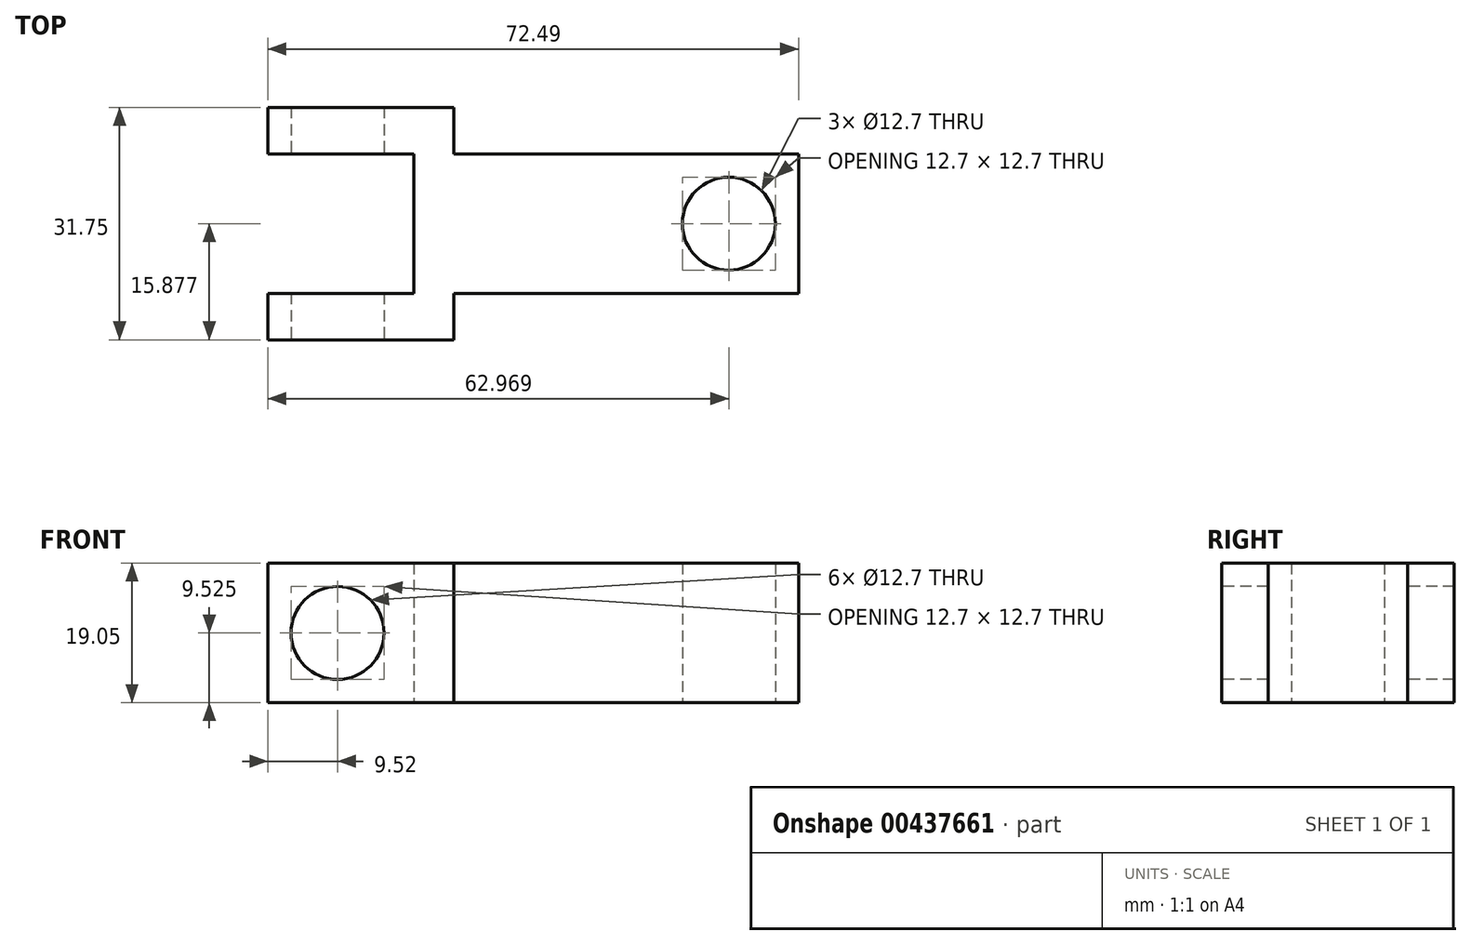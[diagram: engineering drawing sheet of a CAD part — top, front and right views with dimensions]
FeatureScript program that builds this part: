
annotation { "Feature Type Name" : "Feature", "Feature Type Description" : "" }
export const myFeature = defineFeature(function(context is Context, id is Id, definition is map)
    precondition{}
    {
        {
            var Q0;
            Q0=qCreatedBy(makeId("Top.planeOp"),FACE);
            var sketch = newSketch(context, id + "F0", { "sketchPlane" : qUnion([Q0])});
            skLineSegment(sketch, "E0.bottom", {"start": v(-1.7, -4.04) * mm, "end": v(45.4, -4.04) * mm});
            skLineSegment(sketch, "E0.top", {"start": v(-1.7, -23.09) * mm, "end": v(45.4, -23.09) * mm});
            skLineSegment(sketch, "E0.left", {"start": v(-27.1, 2.31) * mm, "end": v(-27.1, -4.04) * mm});
            skLineSegment(sketch, "E0.right", {"start": v(45.4, -4.04) * mm, "end": v(45.4, -23.09) * mm});
            skLineSegment(sketch, "E1", {"start": v(-27.1, 2.31) * mm, "end": v(-1.7, 2.31) * mm});
            skLineSegment(sketch, "E2", {"start": v(-27.1, -29.44) * mm, "end": v(-1.7, -29.44) * mm});
            skLineSegment(sketch, "E3", {"start": v(-1.7, -29.44) * mm, "end": v(-1.7, -23.09) * mm});
            skPoint(sketch, "E4.orphan", {"position": v(0, 2.31) * mm});
            skLineSegment(sketch, "E5.trimOffspring", {"start": v(-1.7, -4.04) * mm, "end": v(-1.7, 2.31) * mm});
            skLineSegment(sketch, "E6.bottom", {"start": v(-27.1, -4.04) * mm, "end": v(-7.15, -4.04) * mm});
            skLineSegment(sketch, "E6.top", {"start": v(-27.1, -23.09) * mm, "end": v(-7.15, -23.09) * mm});
            skLineSegment(sketch, "E6.right", {"start": v(-7.15, -4.04) * mm, "end": v(-7.15, -23.09) * mm});
            skLineSegment(sketch, "E7.trimOffspring", {"start": v(-27.1, -23.09) * mm, "end": v(-27.1, -29.44) * mm});
            skSolve(sketch);
        }
        {
            var Q0;
            Q0=makeQuery(id+"F0.imprint","IMPRINT",FACE,{"disambiguationData":[TD([[makeQuery(id+"F0.imprint","IMPRINT",EDGE,{"derivedFrom":sQuery(id+"F0.wireOp",EDGE,"E0.bottom")}),-1.0]])]});
            extrude(context, id + "F1", {"entities" : qUnion([Q0]), "depth" : 19.05 * mm});
        }
        {
            var Q0;
            Q0=makeQuery(id+"F1.opExtrude","SWEPT_FACE",FACE,{"disambiguationData":[OSD([sQuery(id+"F0.wireOp",EDGE,"E2")])]});
            var sketch = newSketch(context, id + "F2", { "sketchPlane" : qUnion([Q0])});
            skPoint(sketch, "E8", {"position": v(-17.57, 9.53) * mm});
            skSolve(sketch);
        }
        {
            var Q0;
            Q0=sQuery(id+"F2.wireOp",VERTEX,"E8");
            var Q1;
            Q1=makeQuery(id+"F1.opExtrude","SWEPT_BODY",BODY,{"disambiguationData":[OSD([sQuery(id+"F0.wireOp",EDGE,"E0.bottom"),sQuery(id+"F0.wireOp",EDGE,"E0.top"),sQuery(id+"F0.wireOp",EDGE,"E0.left"),sQuery(id+"F0.wireOp",EDGE,"E0.right"),sQuery(id+"F0.wireOp",EDGE,"E1"),sQuery(id+"F0.wireOp",EDGE,"E2"),sQuery(id+"F0.wireOp",EDGE,"E3"),sQuery(id+"F0.wireOp",EDGE,"E5.trimOffspring"),sQuery(id+"F0.wireOp",EDGE,"E6.bottom"),sQuery(id+"F0.wireOp",EDGE,"E6.top"),sQuery(id+"F0.wireOp",EDGE,"E6.right"),sQuery(id+"F0.wireOp",EDGE,"E7.trimOffspring")])]});
            hole(context, id + "F3", {"style" : HoleStyle.SIMPLE, "endStyle" : HoleEndStyle.THROUGH, "holeDiameter" : 12.7 * mm, "isTappedThrough" : true, "tappedDepth" : 12.7 * mm, "tapClearance" : 3, "locations" : qUnion([Q0]), "scope" : qUnion([Q1])});
        }
        {
            var Q0;
            Q0=qCreatedBy(makeId("Top.planeOp"),FACE);
            var sketch = newSketch(context, id + "F4", { "sketchPlane" : qUnion([Q0])});
            skPoint(sketch, "E9", {"position": v(35.88, -13.56) * mm});
            skSolve(sketch);
        }
        {
            var Q0;
            Q0=sQuery(id+"F4.wireOp",VERTEX,"E9");
            var Q1;
            Q1=makeQuery(id+"F1.opExtrude","SWEPT_BODY",BODY,{"disambiguationData":[OSD([sQuery(id+"F0.wireOp",EDGE,"E0.bottom"),sQuery(id+"F0.wireOp",EDGE,"E0.top"),sQuery(id+"F0.wireOp",EDGE,"E0.left"),sQuery(id+"F0.wireOp",EDGE,"E0.right"),sQuery(id+"F0.wireOp",EDGE,"E1"),sQuery(id+"F0.wireOp",EDGE,"E2"),sQuery(id+"F0.wireOp",EDGE,"E3"),sQuery(id+"F0.wireOp",EDGE,"E5.trimOffspring"),sQuery(id+"F0.wireOp",EDGE,"E6.bottom"),sQuery(id+"F0.wireOp",EDGE,"E6.top"),sQuery(id+"F0.wireOp",EDGE,"E6.right"),sQuery(id+"F0.wireOp",EDGE,"E7.trimOffspring")])]});
            hole(context, id + "F5", {"style" : HoleStyle.SIMPLE, "endStyle" : HoleEndStyle.THROUGH, "oppositeDirection" : true, "holeDiameter" : 12.7 * mm, "isTappedThrough" : true, "tappedDepth" : 12.7 * mm, "tapClearance" : 3, "locations" : qUnion([Q0]), "scope" : qUnion([Q1])});
        }
    });
